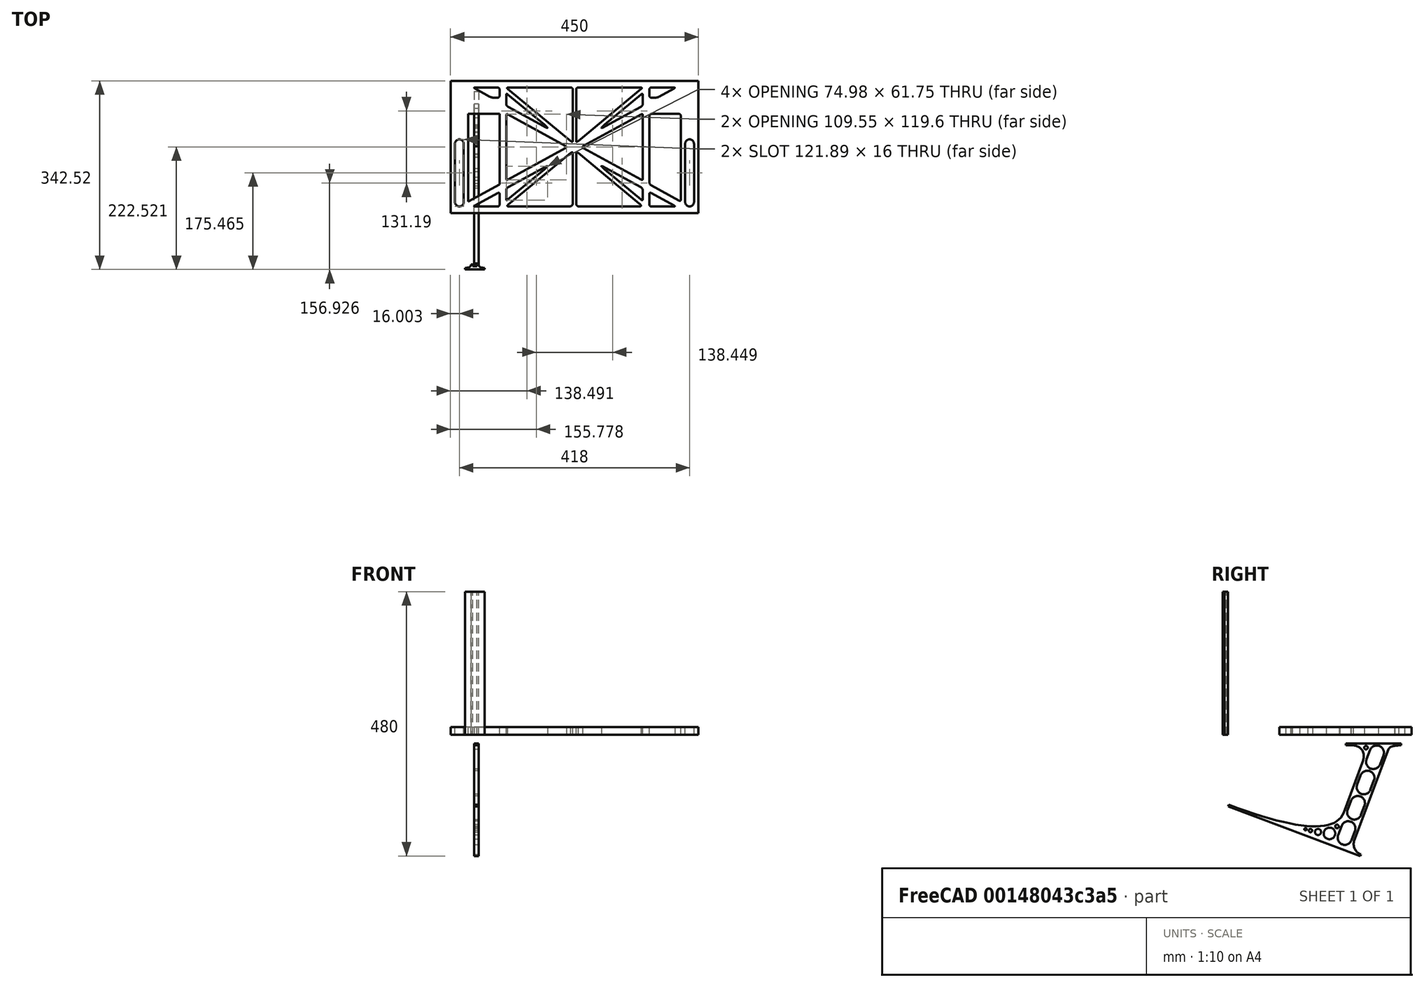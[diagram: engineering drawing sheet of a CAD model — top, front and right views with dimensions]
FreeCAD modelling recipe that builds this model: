
FCSTD DOCUMENT  (FreeCAD 0.19R0.19.2)
Label: laptopStand139FCStd
License: All rights reserved
LicenseURL: http://en.wikipedia.org/wiki/All_rights_reserved
objects: Sketcher::SketchObject×3, Part::Extrusion×3
note: 6 computed .brp shape members not serialized (recipe doc carries the construction recipe); baked Part::Feature solids carry a one-line shape summary decoded from their .brp

FEATURE [Sketcher::SketchObject] Sketch
  FullyConstrained = true
  sketch-geometry (322):
    g0: LineSegment StartX=-10.9272 StartY=-82.7794 StartZ=0 EndX=46.0728 EndY=-51.4823 EndZ=0
    g1: LineSegment StartX=-10.9272 StartY=76.4095 StartZ=0 EndX=-10.9272 EndY=-82.7794 EndZ=0
    g2: LineSegment StartX=46.0728 StartY=76.4095 StartZ=0 EndX=46.0728 EndY=-51.4823 EndZ=0
    g3: LineSegment StartX=-42.9272 StartY=136.221 StartZ=0 EndX=-42.9272 EndY=-103.779 EndZ=0
    g4: LineSegment StartX=407.073 StartY=136.221 StartZ=0 EndX=407.073 EndY=-103.779 EndZ=0
    g5: ArcOfCircle CenterX=-26.9272 CenterY=-83.7794 CenterZ=0 NormalX=0 NormalY=0 NormalZ=1 AngleXU=0 Radius=8 StartAngle=3.14159 EndAngle=6.28319
    g6: ArcOfCircle CenterX=391.073 CenterY=22.1087 CenterZ=0 NormalX=0 NormalY=0 NormalZ=1 AngleXU=0 Radius=8 StartAngle=-4.4e-15 EndAngle=3.14159
    g7: LineSegment StartX=399.073 StartY=22.1087 StartZ=0 EndX=399.073 EndY=-83.7794 EndZ=0
    g8: LineSegment StartX=383.073 StartY=22.1087 StartZ=0 EndX=383.073 EndY=-83.7794 EndZ=0
    g9: ArcOfCircle CenterX=391.073 CenterY=-83.7794 CenterZ=0 NormalX=0 NormalY=0 NormalZ=1 AngleXU=0 Radius=8 StartAngle=3.14159 EndAngle=6.28319
    g10: Circle CenterX=175.022 CenterY=27.0628 CenterZ=0 NormalX=0 NormalY=0 NormalZ=1 AngleXU=0 Radius=1
    g11: Circle CenterX=179.022 CenterY=24.8665 CenterZ=0 NormalX=0 NormalY=0 NormalZ=1 AngleXU=0 Radius=1
    g12: Circle CenterX=179.022 CenterY=27.0628 CenterZ=0 NormalX=0 NormalY=0 NormalZ=1 AngleXU=0 Radius=1
    g13: BSplineCurve PolesCount=3 KnotsCount=2 Degree=2 IsPeriodic=0
    g14: GeomPoint X=175.022 Y=27.0628 Z=0
    g15: GeomPoint X=179.022 Y=27.0628 Z=0
    g16: Circle CenterX=189.124 CenterY=27.0628 CenterZ=0 NormalX=0 NormalY=0 NormalZ=1 AngleXU=0 Radius=1
    g17: Circle CenterX=185.124 CenterY=24.8665 CenterZ=0 NormalX=0 NormalY=0 NormalZ=1 AngleXU=0 Radius=1
    g18: Circle CenterX=185.124 CenterY=27.0628 CenterZ=0 NormalX=0 NormalY=0 NormalZ=1 AngleXU=0 Radius=1
    g19: BSplineCurve PolesCount=3 KnotsCount=2 Degree=2 IsPeriodic=0
    g20: GeomPoint X=189.124 Y=27.0628 Z=0
    g21: GeomPoint X=185.124 Y=27.0628 Z=0
    g22: Circle CenterX=175.022 CenterY=5.37834 CenterZ=0 NormalX=0 NormalY=0 NormalZ=1 AngleXU=0 Radius=1
    g23: Circle CenterX=179.022 CenterY=7.57463 CenterZ=0 NormalX=0 NormalY=0 NormalZ=1 AngleXU=0 Radius=1
    g24: Circle CenterX=179.022 CenterY=5.34704 CenterZ=0 NormalX=0 NormalY=0 NormalZ=1 AngleXU=0 Radius=1
    g25: BSplineCurve PolesCount=3 KnotsCount=2 Degree=2 IsPeriodic=0
    g26: GeomPoint X=175.022 Y=5.37834 Z=0
    g27: GeomPoint X=179.022 Y=5.34704 Z=0
    g28: Circle CenterX=189.124 CenterY=5.37834 CenterZ=0 NormalX=0 NormalY=0 NormalZ=1 AngleXU=0 Radius=1
    g29: Circle CenterX=185.124 CenterY=7.57463 CenterZ=0 NormalX=0 NormalY=0 NormalZ=1 AngleXU=0 Radius=1
    g30: Circle CenterX=185.124 CenterY=5.34704 CenterZ=0 NormalX=0 NormalY=0 NormalZ=1 AngleXU=0 Radius=1
    g31: BSplineCurve PolesCount=3 KnotsCount=2 Degree=2 IsPeriodic=0
    g32: GeomPoint X=189.124 Y=5.37834 Z=0
    g33: GeomPoint X=185.124 Y=5.34704 Z=0
    g34: Circle CenterX=165.871 CenterY=18.1458 CenterZ=0 NormalX=0 NormalY=0 NormalZ=1 AngleXU=0 Radius=1
    g35: Circle CenterX=169.377 CenterY=16.2206 CenterZ=0 NormalX=0 NormalY=0 NormalZ=1 AngleXU=0 Radius=1
    g36: Circle CenterX=165.871 CenterY=14.2954 CenterZ=0 NormalX=0 NormalY=0 NormalZ=1 AngleXU=0 Radius=1
    g37: BSplineCurve PolesCount=3 KnotsCount=2 Degree=2 IsPeriodic=0
    g38: GeomPoint X=165.871 Y=18.1458 Z=0
    g39: GeomPoint X=165.871 Y=14.2954 Z=0
    g40: Circle CenterX=198.275 CenterY=18.1458 CenterZ=0 NormalX=0 NormalY=0 NormalZ=1 AngleXU=0 Radius=1
    g41: Circle CenterX=194.768 CenterY=16.2206 CenterZ=0 NormalX=0 NormalY=0 NormalZ=1 AngleXU=0 Radius=1
    g42: Circle CenterX=198.275 CenterY=14.2954 CenterZ=0 NormalX=0 NormalY=0 NormalZ=1 AngleXU=0 Radius=1
    g43: BSplineCurve PolesCount=3 KnotsCount=2 Degree=2 IsPeriodic=0
    g44: GeomPoint X=198.275 Y=18.1458 Z=0
    g45: GeomPoint X=198.275 Y=14.2954 Z=0
    g46: LineSegment StartX=407.073 StartY=-103.779 StartZ=0 EndX=-42.9272 EndY=-103.779 EndZ=0
    g47: LineSegment StartX=407.073 StartY=136.221 StartZ=0 EndX=-42.9272 EndY=136.221 EndZ=0
    g48: LineSegment StartX=46.0728 StartY=76.4095 StartZ=0 EndX=-10.9272 EndY=76.4095 EndZ=0
    g49: Circle CenterX=125.607 CenterY=54.1951 CenterZ=0 NormalX=0 NormalY=0 NormalZ=1 AngleXU=0 Radius=1
    g50: Circle CenterX=139.632 CenterY=46.4944 CenterZ=0 NormalX=0 NormalY=0 NormalZ=1 AngleXU=0 Radius=1
    g51: Circle CenterX=127.326 CenterY=56.7187 CenterZ=0 NormalX=0 NormalY=0 NormalZ=1 AngleXU=0 Radius=1
    g52: BSplineCurve PolesCount=3 KnotsCount=2 Degree=2 IsPeriodic=0
    g53: GeomPoint X=125.607 Y=54.1951 Z=0
    g54: GeomPoint X=127.326 Y=56.7187 Z=0
    g55: Circle CenterX=236.821 CenterY=56.7187 CenterZ=0 NormalX=0 NormalY=0 NormalZ=1 AngleXU=0 Radius=1
    g56: Circle CenterX=224.513 CenterY=46.4944 CenterZ=0 NormalX=0 NormalY=0 NormalZ=1 AngleXU=0 Radius=1
    g57: Circle CenterX=238.538 CenterY=54.1951 CenterZ=0 NormalX=0 NormalY=0 NormalZ=1 AngleXU=0 Radius=1
    g58: BSplineCurve PolesCount=3 KnotsCount=2 Degree=2 IsPeriodic=0
    g59: GeomPoint X=236.821 Y=56.7187 Z=0
    g60: GeomPoint X=238.538 Y=54.1951 Z=0
    g61: Circle CenterX=238.538 CenterY=-21.7539 CenterZ=0 NormalX=0 NormalY=0 NormalZ=1 AngleXU=0 Radius=1
    g62: Circle CenterX=224.513 CenterY=-14.0532 CenterZ=0 NormalX=0 NormalY=0 NormalZ=1 AngleXU=0 Radius=1
    g63: Circle CenterX=236.821 CenterY=-24.2775 CenterZ=0 NormalX=0 NormalY=0 NormalZ=1 AngleXU=0 Radius=1
    g64: BSplineCurve PolesCount=3 KnotsCount=2 Degree=2 IsPeriodic=0
    g65: GeomPoint X=238.538 Y=-21.7539 Z=0
    g66: GeomPoint X=236.821 Y=-24.2775 Z=0
    g67: Circle CenterX=125.607 CenterY=-21.7539 CenterZ=0 NormalX=0 NormalY=0 NormalZ=1 AngleXU=0 Radius=1
    g68: Circle CenterX=139.632 CenterY=-14.0532 CenterZ=0 NormalX=0 NormalY=0 NormalZ=1 AngleXU=0 Radius=1
    g69: Circle CenterX=127.325 CenterY=-24.2775 CenterZ=0 NormalX=0 NormalY=0 NormalZ=1 AngleXU=0 Radius=1
    g70: BSplineCurve PolesCount=3 KnotsCount=2 Degree=2 IsPeriodic=0
    g71: GeomPoint X=125.607 Y=-21.7539 Z=0
    g72: GeomPoint X=127.325 Y=-24.2775 Z=0
    g73: Circle CenterX=302.996 CenterY=111.695 CenterZ=0 NormalX=0 NormalY=0 NormalZ=1 AngleXU=0 Radius=1
    g74: Circle CenterX=306.073 CenterY=114.251 CenterZ=0 NormalX=0 NormalY=0 NormalZ=1 AngleXU=0 Radius=1
    g75: Circle CenterX=306.073 CenterY=110.251 CenterZ=0 NormalX=0 NormalY=0 NormalZ=1 AngleXU=0 Radius=1
    g76: BSplineCurve PolesCount=3 KnotsCount=2 Degree=2 IsPeriodic=0
    g77: GeomPoint X=302.996 Y=111.695 Z=0
    g78: GeomPoint X=306.073 Y=110.251 Z=0
    g79: Circle CenterX=306.073 CenterY=95.2763 CenterZ=0 NormalX=0 NormalY=0 NormalZ=1 AngleXU=0 Radius=1
    g80: Circle CenterX=306.073 CenterY=91.2763 CenterZ=0 NormalX=0 NormalY=0 NormalZ=1 AngleXU=0 Radius=1
    g81: Circle CenterX=302.567 CenterY=89.3511 CenterZ=0 NormalX=0 NormalY=0 NormalZ=1 AngleXU=0 Radius=1
    g82: BSplineCurve PolesCount=3 KnotsCount=2 Degree=2 IsPeriodic=0
    g83: GeomPoint X=306.073 Y=95.2763 Z=0
    g84: GeomPoint X=302.567 Y=89.3511 Z=0
    g85: LineSegment StartX=306.073 StartY=110.251 StartZ=0 EndX=306.073 EndY=95.2763 EndZ=0
    g86: LineSegment StartX=302.996 StartY=111.695 StartZ=0 EndX=236.821 EndY=56.7187 EndZ=0
    g87: LineSegment StartX=238.538 StartY=54.1951 StartZ=0 EndX=302.567 EndY=89.3511 EndZ=0
    g88: Circle CenterX=61.1496 CenterY=111.695 CenterZ=0 NormalX=0 NormalY=0 NormalZ=1 AngleXU=0 Radius=1
    g89: Circle CenterX=58.0728 CenterY=114.251 CenterZ=0 NormalX=0 NormalY=0 NormalZ=1 AngleXU=0 Radius=1
    g90: Circle CenterX=58.0728 CenterY=110.251 CenterZ=0 NormalX=0 NormalY=0 NormalZ=1 AngleXU=0 Radius=1
    g91: BSplineCurve PolesCount=3 KnotsCount=2 Degree=2 IsPeriodic=0
    g92: GeomPoint X=61.1496 Y=111.695 Z=0
    g93: GeomPoint X=58.0728 Y=110.251 Z=0
    g94: Circle CenterX=61.5791 CenterY=89.3511 CenterZ=0 NormalX=0 NormalY=0 NormalZ=1 AngleXU=0 Radius=1
    g95: Circle CenterX=58.0728 CenterY=91.2763 CenterZ=0 NormalX=0 NormalY=0 NormalZ=1 AngleXU=0 Radius=1
    g96: Circle CenterX=58.0728 CenterY=95.2763 CenterZ=0 NormalX=0 NormalY=0 NormalZ=1 AngleXU=0 Radius=1
    g97: BSplineCurve PolesCount=3 KnotsCount=2 Degree=2 IsPeriodic=0
    g98: GeomPoint X=61.5791 Y=89.3511 Z=0
    g99: GeomPoint X=58.0728 Y=95.2763 Z=0
    g100: LineSegment StartX=58.0728 StartY=110.251 StartZ=0 EndX=58.0728 EndY=95.2763 EndZ=0
    g101: LineSegment StartX=61.1496 StartY=111.695 StartZ=0 EndX=127.326 EndY=56.7187 EndZ=0
    g102: LineSegment StartX=125.607 StartY=54.1951 StartZ=0 EndX=61.5791 EndY=89.3511 EndZ=0
    g103: Circle CenterX=61.5791 CenterY=-56.9099 CenterZ=0 NormalX=0 NormalY=0 NormalZ=1 AngleXU=0 Radius=1
    g104: Circle CenterX=58.0728 CenterY=-58.8351 CenterZ=0 NormalX=0 NormalY=0 NormalZ=1 AngleXU=0 Radius=1
    g105: Circle CenterX=58.0728 CenterY=-62.8351 CenterZ=0 NormalX=0 NormalY=0 NormalZ=1 AngleXU=0 Radius=1
    g106: BSplineCurve PolesCount=3 KnotsCount=2 Degree=2 IsPeriodic=0
    g107: GeomPoint X=61.5791 Y=-56.9099 Z=0
    g108: GeomPoint X=58.0728 Y=-62.8351 Z=0
    g109: Circle CenterX=58.0728 CenterY=-77.8102 CenterZ=0 NormalX=0 NormalY=0 NormalZ=1 AngleXU=0 Radius=1
    g110: Circle CenterX=58.0728 CenterY=-81.8102 CenterZ=0 NormalX=0 NormalY=0 NormalZ=1 AngleXU=0 Radius=1
    g111: Circle CenterX=61.1496 CenterY=-79.2541 CenterZ=0 NormalX=0 NormalY=0 NormalZ=1 AngleXU=0 Radius=1
    g112: BSplineCurve PolesCount=3 KnotsCount=2 Degree=2 IsPeriodic=0
    g113: GeomPoint X=58.0728 Y=-77.8102 Z=0
    g114: GeomPoint X=61.1496 Y=-79.2541 Z=0
    g115: LineSegment StartX=58.0728 StartY=-62.8351 StartZ=0 EndX=58.0728 EndY=-77.8102 EndZ=0
    g116: LineSegment StartX=61.1496 StartY=-79.2541 StartZ=0 EndX=127.325 EndY=-24.2775 EndZ=0
    g117: LineSegment StartX=125.607 StartY=-21.7539 StartZ=0 EndX=61.5791 EndY=-56.9099 EndZ=0
    g118: Circle CenterX=302.567 CenterY=-56.9099 CenterZ=0 NormalX=0 NormalY=0 NormalZ=1 AngleXU=0 Radius=1
    g119: Circle CenterX=306.073 CenterY=-58.8351 CenterZ=0 NormalX=0 NormalY=0 NormalZ=1 AngleXU=0 Radius=1
    g120: Circle CenterX=306.073 CenterY=-62.8351 CenterZ=0 NormalX=0 NormalY=0 NormalZ=1 AngleXU=0 Radius=1
    g121: BSplineCurve PolesCount=3 KnotsCount=2 Degree=2 IsPeriodic=0
    g122: GeomPoint X=302.567 Y=-56.9099 Z=0
    g123: GeomPoint X=306.073 Y=-62.8351 Z=0
    g124: Circle CenterX=302.996 CenterY=-79.2541 CenterZ=0 NormalX=0 NormalY=0 NormalZ=1 AngleXU=0 Radius=1
    g125: Circle CenterX=306.073 CenterY=-81.8102 CenterZ=0 NormalX=0 NormalY=0 NormalZ=1 AngleXU=0 Radius=1
    g126: Circle CenterX=306.073 CenterY=-77.8102 CenterZ=0 NormalX=0 NormalY=0 NormalZ=1 AngleXU=0 Radius=1
    g127: BSplineCurve PolesCount=3 KnotsCount=2 Degree=2 IsPeriodic=0
    g128: GeomPoint X=302.996 Y=-79.2541 Z=0
    g129: GeomPoint X=306.073 Y=-77.8102 Z=0
    g130: LineSegment StartX=306.073 StartY=-62.8351 StartZ=0 EndX=306.073 EndY=-77.8102 EndZ=0
    g131: LineSegment StartX=302.996 StartY=-79.2541 StartZ=0 EndX=236.821 EndY=-24.2775 EndZ=0
    g132: LineSegment StartX=238.538 StartY=-21.7539 StartZ=0 EndX=302.567 EndY=-56.9099 EndZ=0
    g133: Circle CenterX=61.6457 CenterY=-88.8112 CenterZ=0 NormalX=0 NormalY=0 NormalZ=1 AngleXU=0 Radius=1
    g134: Circle CenterX=58.0728 CenterY=-91.7794 CenterZ=0 NormalX=0 NormalY=0 NormalZ=1 AngleXU=0 Radius=1
    g135: Circle CenterX=63.9135 CenterY=-91.7794 CenterZ=0 NormalX=0 NormalY=0 NormalZ=1 AngleXU=0 Radius=1
    g136: BSplineCurve PolesCount=3 KnotsCount=2 Degree=2 IsPeriodic=0
    g137: GeomPoint X=61.6457 Y=-88.8112 Z=0
    g138: GeomPoint X=63.9135 Y=-91.7794 Z=0
    g139: Circle CenterX=179.022 CenterY=-85.8163 CenterZ=0 NormalX=0 NormalY=0 NormalZ=1 AngleXU=0 Radius=1
    g140: Circle CenterX=179.022 CenterY=-91.7794 CenterZ=0 NormalX=0 NormalY=0 NormalZ=1 AngleXU=0 Radius=1
    g141: Circle CenterX=171.895 CenterY=-91.7794 CenterZ=0 NormalX=0 NormalY=0 NormalZ=1 AngleXU=0 Radius=1
    g142: BSplineCurve PolesCount=3 KnotsCount=2 Degree=2 IsPeriodic=0
    g143: GeomPoint X=179.022 Y=-85.8163 Z=0
    g144: GeomPoint X=171.895 Y=-91.7794 Z=0
    g145: Circle CenterX=185.124 CenterY=-86.2028 CenterZ=0 NormalX=0 NormalY=0 NormalZ=1 AngleXU=0 Radius=1
    g146: Circle CenterX=185.124 CenterY=-91.7794 CenterZ=0 NormalX=0 NormalY=0 NormalZ=1 AngleXU=0 Radius=1
    g147: Circle CenterX=191.747 CenterY=-91.7794 CenterZ=0 NormalX=0 NormalY=0 NormalZ=1 AngleXU=0 Radius=1
    g148: BSplineCurve PolesCount=3 KnotsCount=2 Degree=2 IsPeriodic=0
    g149: GeomPoint X=185.124 Y=-86.2028 Z=0
    g150: GeomPoint X=191.747 Y=-91.7794 Z=0
    g151: Circle CenterX=299.888 CenterY=-86.6413 CenterZ=0 NormalX=0 NormalY=0 NormalZ=1 AngleXU=0 Radius=1
    g152: Circle CenterX=306.073 CenterY=-91.7794 CenterZ=0 NormalX=0 NormalY=0 NormalZ=1 AngleXU=0 Radius=1
    g153: Circle CenterX=298.776 CenterY=-91.7794 CenterZ=0 NormalX=0 NormalY=0 NormalZ=1 AngleXU=0 Radius=1
    g154: BSplineCurve PolesCount=3 KnotsCount=2 Degree=2 IsPeriodic=0
    g155: GeomPoint X=299.888 Y=-86.6413 Z=0
    g156: GeomPoint X=298.776 Y=-91.7794 Z=0
    g157: LineSegment StartX=189.124 StartY=5.37834 StartZ=0 EndX=299.888 EndY=-86.6413 EndZ=0
    g158: LineSegment StartX=298.776 StartY=-91.7794 StartZ=0 EndX=191.747 EndY=-91.7794 EndZ=0
    g159: LineSegment StartX=185.124 StartY=-86.2028 StartZ=0 EndX=185.124 EndY=5.34704 EndZ=0
    g160: LineSegment StartX=179.022 StartY=5.34704 StartZ=0 EndX=179.022 EndY=-85.8163 EndZ=0
    g161: LineSegment StartX=171.895 StartY=-91.7794 StartZ=0 EndX=63.9135 EndY=-91.7794 EndZ=0
    g162: LineSegment StartX=61.6457 StartY=-88.8112 StartZ=0 EndX=175.022 EndY=5.37834 EndZ=0
    g163: Circle CenterX=302.073 CenterY=124.221 CenterZ=0 NormalX=0 NormalY=0 NormalZ=1 AngleXU=0 Radius=1
    g164: Circle CenterX=306.073 CenterY=124.221 CenterZ=0 NormalX=0 NormalY=0 NormalZ=1 AngleXU=0 Radius=1
    g165: Circle CenterX=302.996 CenterY=121.665 CenterZ=0 NormalX=0 NormalY=0 NormalZ=1 AngleXU=0 Radius=1
    g166: BSplineCurve PolesCount=3 KnotsCount=2 Degree=2 IsPeriodic=0
    g167: GeomPoint X=302.073 Y=124.221 Z=0
    g168: GeomPoint X=302.996 Y=121.665 Z=0
    g169: Circle CenterX=189.124 CenterY=124.221 CenterZ=0 NormalX=0 NormalY=0 NormalZ=1 AngleXU=0 Radius=1
    g170: Circle CenterX=185.124 CenterY=124.221 CenterZ=0 NormalX=0 NormalY=0 NormalZ=1 AngleXU=0 Radius=1
    g171: Circle CenterX=185.124 CenterY=120.221 CenterZ=0 NormalX=0 NormalY=0 NormalZ=1 AngleXU=0 Radius=1
    g172: BSplineCurve PolesCount=3 KnotsCount=2 Degree=2 IsPeriodic=0
    g173: GeomPoint X=189.124 Y=124.221 Z=0
    g174: GeomPoint X=185.124 Y=120.221 Z=0
    g175: Circle CenterX=175.022 CenterY=124.221 CenterZ=0 NormalX=0 NormalY=0 NormalZ=1 AngleXU=0 Radius=1
    g176: Circle CenterX=179.022 CenterY=124.221 CenterZ=0 NormalX=0 NormalY=0 NormalZ=1 AngleXU=0 Radius=1
    g177: Circle CenterX=179.022 CenterY=120.221 CenterZ=0 NormalX=0 NormalY=0 NormalZ=1 AngleXU=0 Radius=1
    g178: BSplineCurve PolesCount=3 KnotsCount=2 Degree=2 IsPeriodic=0
    g179: GeomPoint X=175.022 Y=124.221 Z=0
    g180: GeomPoint X=179.022 Y=120.221 Z=0
    g181: Circle CenterX=62.0728 CenterY=124.221 CenterZ=0 NormalX=0 NormalY=0 NormalZ=1 AngleXU=0 Radius=1
    g182: Circle CenterX=58.0728 CenterY=124.221 CenterZ=0 NormalX=0 NormalY=0 NormalZ=1 AngleXU=0 Radius=1
    g183: Circle CenterX=61.1496 CenterY=121.665 CenterZ=0 NormalX=0 NormalY=0 NormalZ=1 AngleXU=0 Radius=1
    g184: BSplineCurve PolesCount=3 KnotsCount=2 Degree=2 IsPeriodic=0
    g185: GeomPoint X=62.0728 Y=124.221 Z=0
    g186: GeomPoint X=61.1496 Y=121.665 Z=0
    g187: LineSegment StartX=62.0728 StartY=124.221 StartZ=0 EndX=175.022 EndY=124.221 EndZ=0
    g188: LineSegment StartX=179.022 StartY=120.221 StartZ=0 EndX=179.022 EndY=27.0628 EndZ=0
    g189: LineSegment StartX=185.124 StartY=27.0628 StartZ=0 EndX=185.124 EndY=120.221 EndZ=0
    g190: LineSegment StartX=189.124 StartY=124.221 StartZ=0 EndX=302.073 EndY=124.221 EndZ=0
    g191: LineSegment StartX=302.996 StartY=121.665 StartZ=0 EndX=189.124 EndY=27.0628 EndZ=0
    g192: LineSegment StartX=175.022 StartY=27.0628 StartZ=0 EndX=61.1496 EndY=121.665 EndZ=0
    g193: Circle CenterX=61.5791 CenterY=75.4095 CenterZ=0 NormalX=0 NormalY=0 NormalZ=1 AngleXU=0 Radius=1
    g194: Circle CenterX=58.0728 CenterY=77.3346 CenterZ=0 NormalX=0 NormalY=0 NormalZ=1 AngleXU=0 Radius=1
    g195: Circle CenterX=58.0728 CenterY=73.3346 CenterZ=0 NormalX=0 NormalY=0 NormalZ=1 AngleXU=0 Radius=1
    g196: BSplineCurve PolesCount=3 KnotsCount=2 Degree=2 IsPeriodic=0
    g197: GeomPoint X=61.5791 Y=75.4095 Z=0
    g198: GeomPoint X=58.0728 Y=73.3346 Z=0
    g199: Circle CenterX=58.0728 CenterY=-40.8935 CenterZ=0 NormalX=0 NormalY=0 NormalZ=1 AngleXU=0 Radius=1
    g200: Circle CenterX=58.0728 CenterY=-44.8935 CenterZ=0 NormalX=0 NormalY=0 NormalZ=1 AngleXU=0 Radius=1
    g201: Circle CenterX=61.5791 CenterY=-42.9683 CenterZ=0 NormalX=0 NormalY=0 NormalZ=1 AngleXU=0 Radius=1
    g202: BSplineCurve PolesCount=3 KnotsCount=2 Degree=2 IsPeriodic=0
    g203: GeomPoint X=58.0728 Y=-40.8935 Z=0
    g204: GeomPoint X=61.5791 Y=-42.9683 Z=0
    g205: LineSegment StartX=61.5791 StartY=-42.9683 StartZ=0 EndX=165.871 EndY=14.2954 EndZ=0
    g206: LineSegment StartX=165.871 StartY=18.1458 StartZ=0 EndX=61.5791 EndY=75.4095 EndZ=0
    g207: LineSegment StartX=58.0728 StartY=73.3346 StartZ=0 EndX=58.0728 EndY=-40.8935 EndZ=0
    g208: Circle CenterX=302.567 CenterY=-42.9683 CenterZ=0 NormalX=0 NormalY=0 NormalZ=1 AngleXU=0 Radius=1
    g209: Circle CenterX=306.073 CenterY=-44.8935 CenterZ=0 NormalX=0 NormalY=0 NormalZ=1 AngleXU=0 Radius=1
    g210: Circle CenterX=306.073 CenterY=-40.8935 CenterZ=0 NormalX=0 NormalY=0 NormalZ=1 AngleXU=0 Radius=1
    g211: BSplineCurve PolesCount=3 KnotsCount=2 Degree=2 IsPeriodic=0
    g212: GeomPoint X=302.567 Y=-42.9683 Z=0
    g213: GeomPoint X=306.073 Y=-40.8935 Z=0
    g214: Circle CenterX=306.073 CenterY=73.3346 CenterZ=0 NormalX=0 NormalY=0 NormalZ=1 AngleXU=0 Radius=1
    g215: Circle CenterX=306.073 CenterY=77.3346 CenterZ=0 NormalX=0 NormalY=0 NormalZ=1 AngleXU=0 Radius=1
    g216: Circle CenterX=302.567 CenterY=75.4095 CenterZ=0 NormalX=0 NormalY=0 NormalZ=1 AngleXU=0 Radius=1
    g217: BSplineCurve PolesCount=3 KnotsCount=2 Degree=2 IsPeriodic=0
    g218: GeomPoint X=306.073 Y=73.3346 Z=0
    g219: GeomPoint X=302.567 Y=75.4095 Z=0
    g220: LineSegment StartX=302.567 StartY=-42.9683 StartZ=0 EndX=198.275 EndY=14.2954 EndZ=0
    g221: LineSegment StartX=198.275 StartY=18.1458 StartZ=0 EndX=302.567 EndY=75.4095 EndZ=0
    g222: LineSegment StartX=306.073 StartY=73.3346 StartZ=0 EndX=306.073 EndY=-40.8935 EndZ=0
    g223: LineSegment StartX=322.073 StartY=105.865 StartZ=0 EndX=328.643 EndY=105.865 EndZ=0
    g224: LineSegment StartX=318.073 StartY=120.221 StartZ=0 EndX=318.073 EndY=109.865 EndZ=0
    g225: LineSegment StartX=336.157 StartY=107.779 StartZ=0 EndX=362.567 EndY=122.294 EndZ=0
    g226: Circle CenterX=362.073 CenterY=124.221 CenterZ=0 NormalX=0 NormalY=0 NormalZ=1 AngleXU=0 Radius=1
    g227: Circle CenterX=366.073 CenterY=124.221 CenterZ=0 NormalX=0 NormalY=0 NormalZ=1 AngleXU=0 Radius=1
    g228: Circle CenterX=362.567 CenterY=122.294 CenterZ=0 NormalX=0 NormalY=0 NormalZ=1 AngleXU=0 Radius=1
    g229: BSplineCurve PolesCount=3 KnotsCount=2 Degree=2 IsPeriodic=0
    g230: GeomPoint X=362.073 Y=124.221 Z=0
    g231: GeomPoint X=362.567 Y=122.294 Z=0
    g232: Circle CenterX=322.073 CenterY=124.221 CenterZ=0 NormalX=0 NormalY=0 NormalZ=1 AngleXU=0 Radius=1
    g233: Circle CenterX=318.073 CenterY=124.221 CenterZ=0 NormalX=0 NormalY=0 NormalZ=1 AngleXU=0 Radius=1
    g234: Circle CenterX=318.073 CenterY=120.221 CenterZ=0 NormalX=0 NormalY=0 NormalZ=1 AngleXU=0 Radius=1
    g235: BSplineCurve PolesCount=3 KnotsCount=2 Degree=2 IsPeriodic=0
    g236: GeomPoint X=322.073 Y=124.221 Z=0
    g237: GeomPoint X=318.073 Y=120.221 Z=0
    g238: Circle CenterX=322.073 CenterY=105.865 CenterZ=0 NormalX=0 NormalY=0 NormalZ=1 AngleXU=0 Radius=1
    g239: Circle CenterX=318.073 CenterY=105.865 CenterZ=0 NormalX=0 NormalY=0 NormalZ=1 AngleXU=0 Radius=1
    g240: Circle CenterX=318.073 CenterY=109.865 CenterZ=0 NormalX=0 NormalY=0 NormalZ=1 AngleXU=0 Radius=1
    g241: BSplineCurve PolesCount=3 KnotsCount=2 Degree=2 IsPeriodic=0
    g242: GeomPoint X=322.073 Y=105.865 Z=0
    g243: GeomPoint X=318.073 Y=109.865 Z=0
    g244: Circle CenterX=336.157 CenterY=107.779 CenterZ=0 NormalX=0 NormalY=0 NormalZ=1 AngleXU=0 Radius=1
    g245: Circle CenterX=332.651 CenterY=105.853 CenterZ=0 NormalX=0 NormalY=0 NormalZ=1 AngleXU=0 Radius=1
    g246: Circle CenterX=328.643 CenterY=105.865 CenterZ=0 NormalX=0 NormalY=0 NormalZ=1 AngleXU=0 Radius=1
    g247: BSplineCurve PolesCount=3 KnotsCount=2 Degree=2 IsPeriodic=0
    g248: GeomPoint X=336.157 Y=107.779 Z=0
    g249: GeomPoint X=328.643 Y=105.865 Z=0
    g250: LineSegment StartX=322.073 StartY=124.221 StartZ=0 EndX=362.073 EndY=124.221 EndZ=0
    g251: Circle CenterX=371.567 CenterY=-80.8644 CenterZ=0 NormalX=0 NormalY=0 NormalZ=1 AngleXU=0 Radius=1
    g252: Circle CenterX=375.073 CenterY=-82.7896 CenterZ=0 NormalX=0 NormalY=0 NormalZ=1 AngleXU=0 Radius=1
    g253: Circle CenterX=375.073 CenterY=-78.7896 CenterZ=0 NormalX=0 NormalY=0 NormalZ=1 AngleXU=0 Radius=1
    g254: BSplineCurve PolesCount=3 KnotsCount=2 Degree=2 IsPeriodic=0
    g255: GeomPoint X=371.567 Y=-80.8644 Z=0
    g256: GeomPoint X=375.073 Y=-78.7896 Z=0
    g257: Circle CenterX=321.579 CenterY=-53.4075 CenterZ=0 NormalX=0 NormalY=0 NormalZ=1 AngleXU=0 Radius=1
    g258: Circle CenterX=318.073 CenterY=-51.4823 CenterZ=0 NormalX=0 NormalY=0 NormalZ=1 AngleXU=0 Radius=1
    g259: Circle CenterX=318.073 CenterY=-47.4805 CenterZ=0 NormalX=0 NormalY=0 NormalZ=1 AngleXU=0 Radius=1
    g260: BSplineCurve PolesCount=3 KnotsCount=2 Degree=2 IsPeriodic=0
    g261: GeomPoint X=321.579 Y=-53.4075 Z=0
    g262: GeomPoint X=318.073 Y=-47.4805 Z=0
    g263: LineSegment StartX=371.567 StartY=-80.8644 StartZ=0 EndX=321.579 EndY=-53.4075 EndZ=0
    g264: Circle CenterX=321.579 CenterY=-67.3492 CenterZ=0 NormalX=0 NormalY=0 NormalZ=1 AngleXU=0 Radius=1
    g265: Circle CenterX=318.073 CenterY=-65.424 CenterZ=0 NormalX=0 NormalY=0 NormalZ=1 AngleXU=0 Radius=1
    g266: Circle CenterX=318.073 CenterY=-69.424 CenterZ=0 NormalX=0 NormalY=0 NormalZ=1 AngleXU=0 Radius=1
    g267: BSplineCurve PolesCount=3 KnotsCount=2 Degree=2 IsPeriodic=0
    g268: GeomPoint X=321.579 Y=-67.3492 Z=0
    g269: GeomPoint X=318.073 Y=-69.424 Z=0
    g270: Circle CenterX=362.567 CenterY=-89.8542 CenterZ=0 NormalX=0 NormalY=0 NormalZ=1 AngleXU=0 Radius=1
    g271: Circle CenterX=366.073 CenterY=-91.7794 CenterZ=0 NormalX=0 NormalY=0 NormalZ=1 AngleXU=0 Radius=1
    g272: Circle CenterX=362.073 CenterY=-91.7794 CenterZ=0 NormalX=0 NormalY=0 NormalZ=1 AngleXU=0 Radius=1
    g273: BSplineCurve PolesCount=3 KnotsCount=2 Degree=2 IsPeriodic=0
    g274: GeomPoint X=362.567 Y=-89.8542 Z=0
    g275: GeomPoint X=362.073 Y=-91.7794 Z=0
    g276: Circle CenterX=322.073 CenterY=-91.7794 CenterZ=0 NormalX=0 NormalY=0 NormalZ=1 AngleXU=0 Radius=1
    g277: Circle CenterX=318.073 CenterY=-91.7794 CenterZ=0 NormalX=0 NormalY=0 NormalZ=1 AngleXU=0 Radius=1
    g278: Circle CenterX=318.073 CenterY=-87.7794 CenterZ=0 NormalX=0 NormalY=0 NormalZ=1 AngleXU=0 Radius=1
    g279: BSplineCurve PolesCount=3 KnotsCount=2 Degree=2 IsPeriodic=0
    g280: GeomPoint X=322.073 Y=-91.7794 Z=0
    g281: GeomPoint X=318.073 Y=-87.7794 Z=0
    g282: LineSegment StartX=362.567 StartY=-89.8542 StartZ=0 EndX=321.579 EndY=-67.3492 EndZ=0
    g283: LineSegment StartX=318.073 StartY=-69.424 StartZ=0 EndX=318.073 EndY=-87.7794 EndZ=0
    g284: LineSegment StartX=322.073 StartY=-91.7794 StartZ=0 EndX=362.073 EndY=-91.7794 EndZ=0
    g285: Circle CenterX=42.5666 CenterY=-67.3492 CenterZ=0 NormalX=0 NormalY=0 NormalZ=1 AngleXU=0 Radius=1
    g286: Circle CenterX=46.0728 CenterY=-65.424 CenterZ=0 NormalX=0 NormalY=0 NormalZ=1 AngleXU=0 Radius=1
    g287: Circle CenterX=46.0728 CenterY=-69.424 CenterZ=0 NormalX=0 NormalY=0 NormalZ=1 AngleXU=0 Radius=1
    g288: BSplineCurve PolesCount=3 KnotsCount=2 Degree=2 IsPeriodic=0
    g289: GeomPoint X=42.5666 Y=-67.3492 Z=0
    g290: GeomPoint X=46.0728 Y=-69.424 Z=0
    g291: Circle CenterX=46.0728 CenterY=-87.7794 CenterZ=0 NormalX=0 NormalY=0 NormalZ=1 AngleXU=0 Radius=1
    g292: Circle CenterX=46.0728 CenterY=-91.7794 CenterZ=0 NormalX=0 NormalY=0 NormalZ=1 AngleXU=0 Radius=1
    g293: Circle CenterX=42.0728 CenterY=-91.7794 CenterZ=0 NormalX=0 NormalY=0 NormalZ=1 AngleXU=0 Radius=1
    g294: BSplineCurve PolesCount=3 KnotsCount=2 Degree=2 IsPeriodic=0
    g295: GeomPoint X=46.0728 Y=-87.7794 Z=0
    g296: GeomPoint X=42.0728 Y=-91.7794 Z=0
    g297: Circle CenterX=2.07281 CenterY=-91.7794 CenterZ=0 NormalX=0 NormalY=0 NormalZ=1 AngleXU=0 Radius=1
    g298: Circle CenterX=-1.92719 CenterY=-91.7794 CenterZ=0 NormalX=0 NormalY=0 NormalZ=1 AngleXU=0 Radius=1
    g299: Circle CenterX=1.57905 CenterY=-89.8542 CenterZ=0 NormalX=0 NormalY=0 NormalZ=1 AngleXU=0 Radius=1
    g300: BSplineCurve PolesCount=3 KnotsCount=2 Degree=2 IsPeriodic=0
    g301: GeomPoint X=2.07281 Y=-91.7794 Z=0
    g302: GeomPoint X=1.57905 Y=-89.8542 Z=0
    g303: LineSegment StartX=2.07281 StartY=-91.7794 StartZ=0 EndX=42.0728 EndY=-91.7794 EndZ=0
    g304: LineSegment StartX=46.0728 StartY=-87.7794 StartZ=0 EndX=46.0728 EndY=-69.424 EndZ=0
    g305: LineSegment StartX=42.5666 StartY=-67.3492 StartZ=0 EndX=1.57905 EndY=-89.8542 EndZ=0
    g306: Circle CenterX=322.073 CenterY=76.4095 CenterZ=0 NormalX=0 NormalY=0 NormalZ=1 AngleXU=0 Radius=4
    g307: BSplineCurve PolesCount=3 KnotsCount=2 Degree=2 IsPeriodic=0
    g308: GeomPoint X=318.073 Y=72.4095 Z=0
    g309: GeomPoint X=322.073 Y=76.4095 Z=0
    g310: Circle CenterX=375.073 CenterY=72.4095 CenterZ=0 NormalX=0 NormalY=0 NormalZ=1 AngleXU=0 Radius=1
    g311: Circle CenterX=375.073 CenterY=76.4095 CenterZ=0 NormalX=0 NormalY=0 NormalZ=1 AngleXU=0 Radius=1
    g312: Circle CenterX=371.073 CenterY=76.4095 CenterZ=0 NormalX=0 NormalY=0 NormalZ=1 AngleXU=0 Radius=1
    g313: BSplineCurve PolesCount=3 KnotsCount=2 Degree=2 IsPeriodic=0
    g314: GeomPoint X=375.073 Y=72.4095 Z=0
    g315: GeomPoint X=371.073 Y=76.4095 Z=0
    g316: LineSegment StartX=322.073 StartY=76.4095 StartZ=0 EndX=371.073 EndY=76.4095 EndZ=0
    g317: LineSegment StartX=318.073 StartY=72.4095 StartZ=0 EndX=318.073 EndY=-47.4805 EndZ=0
    g318: LineSegment StartX=375.073 StartY=72.4095 StartZ=0 EndX=375.073 EndY=-78.7896 EndZ=0
    g319: ArcOfCircle CenterX=-26.9272 CenterY=22.1087 CenterZ=0 NormalX=0 NormalY=0 NormalZ=1 AngleXU=0 Radius=4 StartAngle=5e-16 EndAngle=3.14159
    g320: LineSegment StartX=-30.9272 StartY=22.1087 StartZ=0 EndX=-34.9272 EndY=-83.7794 EndZ=0
    g321: LineSegment StartX=-18.9272 StartY=-83.7794 StartZ=0 EndX=-22.9272 EndY=22.1087 EndZ=0
  constraints (531):
    c: Coincident(g0,g2)
    c: Block(g0)
    c: Block(g1)
    c: Vertical(g3)
    c: Vertical(g4)
    c: Block(g4)
    c: Block(g3)
    c: Tangent(g6,g7) = 1.5708
    c: Tangent(g7,g9) = 1.5708
    c: Equal(g6,g9)
    c: Coincident(g8,g6)
    c: Coincident(g8,g9)
    c: Block(g7)
    c: Block(g8)
    c: Weight(g10) = 1
    c: Equal(g10,g11)
    c: Equal(g10,g12)
    c: InternalAlignment(g10,g13)
    c: InternalAlignment(g11,g13)
    c: InternalAlignment(g12,g13)
    c: InternalAlignment(g14,g13)
    c: InternalAlignment(g15,g13)
    c: Weight(g16) = 1
    c: Equal(g16,g17)
    c: Equal(g16,g18)
    c: InternalAlignment(g16,g19)
    c: InternalAlignment(g17,g19)
    c: InternalAlignment(g18,g19)
    c: InternalAlignment(g20,g19)
    c: InternalAlignment(g21,g19)
    c: Block(g19)
    c: Block(g13)
    c: Weight(g22) = 1
    c: Equal(g22,g23)
    c: Equal(g22,g24)
    c: InternalAlignment(g22,g25)
    c: InternalAlignment(g23,g25)
    c: InternalAlignment(g24,g25)
    c: InternalAlignment(g26,g25)
    c: InternalAlignment(g27,g25)
    c: Weight(g28) = 1
    c: Equal(g28,g29)
    c: Equal(g28,g30)
    c: InternalAlignment(g28,g31)
    c: InternalAlignment(g29,g31)
    c: InternalAlignment(g30,g31)
    c: InternalAlignment(g32,g31)
    c: InternalAlignment(g33,g31)
    c: Block(g31)
    c: Block(g25)
    c: Weight(g34) = 1
    c: Equal(g34,g35)
    c: Equal(g34,g36)
    c: InternalAlignment(g34,g37)
    c: InternalAlignment(g35,g37)
    c: InternalAlignment(g36,g37)
    c: InternalAlignment(g38,g37)
    c: InternalAlignment(g39,g37)
    c: Weight(g40) = 1
    c: Equal(g40,g41)
    c: Equal(g40,g42)
    c: InternalAlignment(g40,g43)
    c: InternalAlignment(g41,g43)
    c: InternalAlignment(g42,g43)
    c: InternalAlignment(g44,g43)
    c: InternalAlignment(g45,g43)
    c: Block(g37)
    c: Block(g43)
    c: Coincident(g46,g4)
    c: Coincident(g46,g3)
    c: Horizontal(g46)
    c: Distance(g46) = 450
    c: Coincident(g47,g4)
    c: Coincident(g47,g3)
    c: Horizontal(g47)
    c: Horizontal(g48)
    c: Coincident(g2,g48)
    c: Block(g48)
    c: Coincident(g1,g48)
    c: Weight(g49) = 1
    c: Equal(g49,g50)
    c: Equal(g49,g51)
    c: InternalAlignment(g49,g52)
    c: InternalAlignment(g50,g52)
    c: InternalAlignment(g51,g52)
    c: InternalAlignment(g53,g52)
    c: InternalAlignment(g54,g52)
    c: Block(g52)
    c: Weight(g55) = 1
    c: Equal(g55,g56)
    c: Equal(g55,g57)
    c: InternalAlignment(g55,g58)
    c: InternalAlignment(g56,g58)
    c: InternalAlignment(g57,g58)
    c: InternalAlignment(g59,g58)
    c: InternalAlignment(g60,g58)
    c: Block(g58)
    c: Weight(g61) = 1
    c: Equal(g61,g62)
    c: Equal(g61,g63)
    c: InternalAlignment(g61,g64)
    c: InternalAlignment(g62,g64)
    c: InternalAlignment(g63,g64)
    c: InternalAlignment(g65,g64)
    c: InternalAlignment(g66,g64)
    c: Block(g64)
    c: Weight(g67) = 1
    c: Equal(g67,g68)
    c: Equal(g67,g69)
    c: InternalAlignment(g67,g70)
    c: InternalAlignment(g68,g70)
    c: InternalAlignment(g69,g70)
    c: InternalAlignment(g71,g70)
    c: InternalAlignment(g72,g70)
    c: Block(g70)
    c: Weight(g73) = 1
    c: Equal(g73,g74)
    c: Equal(g73,g75)
    c: InternalAlignment(g73,g76)
    c: InternalAlignment(g74,g76)
    c: InternalAlignment(g75,g76)
    c: InternalAlignment(g77,g76)
    c: InternalAlignment(g78,g76)
    c: Weight(g79) = 1
    c: Equal(g79,g80)
    c: Equal(g79,g81)
    c: InternalAlignment(g79,g82)
    c: InternalAlignment(g80,g82)
    c: InternalAlignment(g81,g82)
    c: InternalAlignment(g83,g82)
    c: InternalAlignment(g84,g82)
    c: Block(g76)
    c: Block(g82)
    c: Coincident(g85,g76)
    c: Coincident(g85,g82)
    c: Vertical(g85)
    c: Coincident(g86,g76)
    c: Coincident(g86,g58)
    c: Coincident(g87,g58)
    c: Coincident(g87,g82)
    c: Weight(g88) = 1
    c: Equal(g88,g89)
    c: Equal(g88,g90)
    c: InternalAlignment(g88,g91)
    c: InternalAlignment(g89,g91)
    c: InternalAlignment(g90,g91)
    c: InternalAlignment(g92,g91)
    c: InternalAlignment(g93,g91)
    c: Weight(g94) = 1
    c: Equal(g94,g95)
    c: Equal(g94,g96)
    c: InternalAlignment(g94,g97)
    c: InternalAlignment(g95,g97)
    c: InternalAlignment(g96,g97)
    c: InternalAlignment(g98,g97)
    c: InternalAlignment(g99,g97)
    c: Block(g91)
    c: Block(g97)
    c: Coincident(g100,g91)
    c: Coincident(g100,g97)
    c: Vertical(g100)
    c: Coincident(g101,g91)
    c: Coincident(g101,g52)
    c: Coincident(g102,g52)
    c: Coincident(g102,g97)
    c: Weight(g103) = 1
    c: Equal(g103,g104)
    c: Equal(g103,g105)
    c: InternalAlignment(g103,g106)
    c: InternalAlignment(g104,g106)
    c: InternalAlignment(g105,g106)
    c: InternalAlignment(g107,g106)
    c: InternalAlignment(g108,g106)
    c: Weight(g109) = 1
    c: Equal(g109,g110)
    c: Equal(g109,g111)
    c: InternalAlignment(g109,g112)
    c: InternalAlignment(g110,g112)
    c: InternalAlignment(g111,g112)
    c: InternalAlignment(g113,g112)
    c: InternalAlignment(g114,g112)
    c: Block(g106)
    c: Block(g112)
    c: Coincident(g115,g106)
    c: Coincident(g115,g112)
    c: Vertical(g115)
    c: Coincident(g116,g112)
    c: Coincident(g116,g70)
    c: Coincident(g117,g70)
    c: Coincident(g117,g106)
    c: Weight(g118) = 1
    c: Equal(g118,g119)
    c: Equal(g118,g120)
    c: InternalAlignment(g118,g121)
    c: InternalAlignment(g119,g121)
    c: InternalAlignment(g120,g121)
    c: InternalAlignment(g122,g121)
    c: InternalAlignment(g123,g121)
    c: Weight(g124) = 1
    c: Equal(g124,g125)
    c: Equal(g124,g126)
    c: InternalAlignment(g124,g127)
    c: InternalAlignment(g125,g127)
    c: InternalAlignment(g126,g127)
    c: InternalAlignment(g128,g127)
    c: InternalAlignment(g129,g127)
    c: Block(g121)
    c: Block(g127)
    c: Coincident(g130,g121)
    c: Coincident(g130,g127)
    c: Vertical(g130)
    c: Coincident(g131,g127)
    c: Coincident(g131,g64)
    c: Coincident(g132,g64)
    c: Coincident(g132,g121)
    c: Weight(g133) = 1
    c: Equal(g133,g134)
    c: Equal(g133,g135)
    c: InternalAlignment(g133,g136)
    c: InternalAlignment(g134,g136)
    c: InternalAlignment(g135,g136)
    c: InternalAlignment(g137,g136)
    c: InternalAlignment(g138,g136)
    c: Weight(g139) = 1
    c: Equal(g139,g140)
    c: Equal(g139,g141)
    c: InternalAlignment(g139,g142)
    c: InternalAlignment(g140,g142)
    c: InternalAlignment(g141,g142)
    c: InternalAlignment(g143,g142)
    c: InternalAlignment(g144,g142)
    c: Weight(g145) = 1
    c: Equal(g145,g146)
    c: Equal(g145,g147)
    c: InternalAlignment(g145,g148)
    c: InternalAlignment(g146,g148)
    c: InternalAlignment(g147,g148)
    c: InternalAlignment(g149,g148)
    c: InternalAlignment(g150,g148)
    c: Weight(g151) = 1
    c: Equal(g151,g152)
    c: Equal(g151,g153)
    c: InternalAlignment(g151,g154)
    c: InternalAlignment(g152,g154)
    c: InternalAlignment(g153,g154)
    c: InternalAlignment(g155,g154)
    c: InternalAlignment(g156,g154)
    c: Block(g154)
    c: Block(g148)
    c: Block(g142)
    c: Block(g136)
    c: Coincident(g157,g31)
    c: Coincident(g157,g154)
    c: Coincident(g158,g154)
    c: Coincident(g158,g148)
    c: Horizontal(g158)
    c: Coincident(g159,g148)
    c: Coincident(g159,g31)
    c: Vertical(g159)
    c: Coincident(g160,g25)
    c: Coincident(g160,g142)
    c: Vertical(g160)
    c: Coincident(g161,g142)
    c: Coincident(g161,g136)
    c: Horizontal(g161)
    c: Coincident(g162,g136)
    c: Coincident(g162,g25)
    c: Weight(g163) = 1
    c: Equal(g163,g164)
    c: Equal(g163,g165)
    c: InternalAlignment(g163,g166)
    c: InternalAlignment(g164,g166)
    c: InternalAlignment(g165,g166)
    c: InternalAlignment(g167,g166)
    c: InternalAlignment(g168,g166)
    c: Weight(g169) = 1
    c: Equal(g169,g170)
    c: Equal(g169,g171)
    c: InternalAlignment(g169,g172)
    c: InternalAlignment(g170,g172)
    c: InternalAlignment(g171,g172)
    c: InternalAlignment(g173,g172)
    c: InternalAlignment(g174,g172)
    c: Weight(g175) = 1
    c: Equal(g175,g176)
    c: Equal(g175,g177)
    c: InternalAlignment(g175,g178)
    c: InternalAlignment(g176,g178)
    c: InternalAlignment(g177,g178)
    c: InternalAlignment(g179,g178)
    c: InternalAlignment(g180,g178)
    c: Weight(g181) = 1
    c: Equal(g181,g182)
    c: Equal(g181,g183)
    c: InternalAlignment(g181,g184)
    c: InternalAlignment(g182,g184)
    c: InternalAlignment(g183,g184)
    c: InternalAlignment(g185,g184)
    c: InternalAlignment(g186,g184)
    c: Block(g184)
    c: Block(g178)
    c: Block(g172)
    c: Block(g166)
    c: Coincident(g187,g184)
    c: Coincident(g187,g178)
    c: Horizontal(g187)
    c: Coincident(g188,g178)
    c: Coincident(g188,g13)
    c: Vertical(g188)
    c: Coincident(g189,g19)
    c: Coincident(g189,g172)
    c: Vertical(g189)
    c: Coincident(g190,g172)
    c: Coincident(g190,g166)
    c: Horizontal(g190)
    c: Coincident(g191,g166)
    c: Coincident(g191,g19)
    c: Coincident(g192,g13)
    c: Weight(g193) = 1
    c: Equal(g193,g194)
    c: Equal(g193,g195)
    c: InternalAlignment(g193,g196)
    c: InternalAlignment(g194,g196)
    c: InternalAlignment(g195,g196)
    c: InternalAlignment(g197,g196)
    c: InternalAlignment(g198,g196)
    c: Weight(g199) = 1
    c: Equal(g199,g200)
    c: Equal(g199,g201)
    c: InternalAlignment(g199,g202)
    c: InternalAlignment(g200,g202)
    c: InternalAlignment(g201,g202)
    c: InternalAlignment(g203,g202)
    c: InternalAlignment(g204,g202)
    c: Block(g202)
    c: Block(g196)
    c: Coincident(g205,g202)
    c: Coincident(g205,g37)
    c: Coincident(g206,g37)
    c: Coincident(g206,g196)
    c: Coincident(g207,g196)
    c: Coincident(g207,g202)
    c: Vertical(g207)
    c: Weight(g208) = 1
    c: Equal(g208,g209)
    c: Equal(g208,g210)
    c: InternalAlignment(g208,g211)
    c: InternalAlignment(g209,g211)
    c: InternalAlignment(g210,g211)
    c: InternalAlignment(g212,g211)
    c: InternalAlignment(g213,g211)
    c: Weight(g214) = 1
    c: Equal(g214,g215)
    c: Equal(g214,g216)
    c: InternalAlignment(g214,g217)
    c: InternalAlignment(g215,g217)
    c: InternalAlignment(g216,g217)
    c: InternalAlignment(g218,g217)
    c: InternalAlignment(g219,g217)
    c: Block(g217)
    c: Block(g211)
    c: Coincident(g220,g211)
    c: Coincident(g220,g43)
    c: Coincident(g221,g43)
    c: Coincident(g221,g217)
    c: Coincident(g222,g217)
    c: Coincident(g222,g211)
    c: Vertical(g222)
    c: Horizontal(g223)
    c: Block(g223)
    c: Vertical(g224)
    c: Block(g224)
    c: Block(g225)
    c: Weight(g226) = 1
    c: Equal(g226,g227)
    c: Equal(g226,g228)
    c: InternalAlignment(g226,g229)
    c: InternalAlignment(g227,g229)
    c: InternalAlignment(g228,g229)
    c: InternalAlignment(g230,g229)
    c: InternalAlignment(g231,g229)
    c: Weight(g232) = 1
    c: Equal(g232,g233)
    c: Equal(g232,g234)
    c: InternalAlignment(g232,g235)
    c: InternalAlignment(g233,g235)
    c: InternalAlignment(g234,g235)
    c: InternalAlignment(g236,g235)
    c: InternalAlignment(g237,g235)
    c: Weight(g238) = 1
    c: Equal(g238,g239)
    c: Equal(g238,g240)
    c: InternalAlignment(g238,g241)
    c: InternalAlignment(g239,g241)
    c: InternalAlignment(g240,g241)
    c: InternalAlignment(g242,g241)
    c: InternalAlignment(g243,g241)
    c: Weight(g244) = 1
    c: Equal(g244,g245)
    c: Equal(g244,g246)
    c: InternalAlignment(g244,g247)
    c: InternalAlignment(g245,g247)
    c: InternalAlignment(g246,g247)
    c: InternalAlignment(g248,g247)
    c: InternalAlignment(g249,g247)
    c: Block(g229)
    c: Block(g235)
    c: Block(g241)
    c: Block(g247)
    c: Coincident(g250,g235)
    c: Coincident(g250,g229)
    c: Horizontal(g250)
    c: Block(g192)
    c: Weight(g251) = 1
    c: Equal(g251,g252)
    c: Equal(g251,g253)
    c: InternalAlignment(g251,g254)
    c: InternalAlignment(g252,g254)
    c: InternalAlignment(g253,g254)
    c: InternalAlignment(g255,g254)
    c: InternalAlignment(g256,g254)
    c: Weight(g257) = 1
    c: Equal(g257,g258)
    c: Equal(g257,g259)
    c: InternalAlignment(g257,g260)
    c: InternalAlignment(g258,g260)
    c: InternalAlignment(g259,g260)
    c: InternalAlignment(g261,g260)
    c: InternalAlignment(g262,g260)
    c: Block(g254)
    c: Block(g260)
    c: Coincident(g263,g254)
    c: Coincident(g263,g260)
    c: Weight(g264) = 1
    c: Equal(g264,g265)
    c: Equal(g264,g266)
    c: InternalAlignment(g264,g267)
    c: InternalAlignment(g265,g267)
    c: InternalAlignment(g266,g267)
    c: InternalAlignment(g268,g267)
    c: InternalAlignment(g269,g267)
    c: Weight(g270) = 1
    c: Equal(g270,g271)
    c: Equal(g270,g272)
    c: InternalAlignment(g270,g273)
    c: InternalAlignment(g271,g273)
    c: InternalAlignment(g272,g273)
    c: InternalAlignment(g274,g273)
    c: InternalAlignment(g275,g273)
    c: Weight(g276) = 1
    c: Equal(g276,g277)
    c: Equal(g276,g278)
    c: InternalAlignment(g276,g279)
    c: InternalAlignment(g277,g279)
    c: InternalAlignment(g278,g279)
    c: InternalAlignment(g280,g279)
    c: InternalAlignment(g281,g279)
    c: Block(g279)
    c: Block(g273)
    c: Block(g267)
    c: Coincident(g282,g273)
    c: Coincident(g282,g267)
    c: Coincident(g283,g267)
    c: Coincident(g283,g279)
    c: Vertical(g283)
    c: Coincident(g284,g279)
    c: Coincident(g284,g273)
    c: Horizontal(g284)
    c: Weight(g285) = 1
    c: Equal(g285,g286)
    c: Equal(g285,g287)
    c: InternalAlignment(g285,g288)
    c: InternalAlignment(g286,g288)
    c: InternalAlignment(g287,g288)
    c: InternalAlignment(g289,g288)
    c: InternalAlignment(g290,g288)
    c: Weight(g291) = 1
    c: Equal(g291,g292)
    c: Equal(g291,g293)
    c: InternalAlignment(g291,g294)
    c: InternalAlignment(g292,g294)
    c: InternalAlignment(g293,g294)
    c: InternalAlignment(g295,g294)
    c: InternalAlignment(g296,g294)
    c: Weight(g297) = 1
    c: Equal(g297,g298)
    c: Equal(g297,g299)
    c: InternalAlignment(g297,g300)
    c: InternalAlignment(g298,g300)
    c: InternalAlignment(g299,g300)
    c: InternalAlignment(g301,g300)
    c: InternalAlignment(g302,g300)
    c: Block(g300)
    c: Block(g294)
    c: Block(g288)
    c: Coincident(g303,g300)
    c: Coincident(g303,g294)
    c: Horizontal(g303)
    c: Coincident(g304,g294)
    c: Coincident(g304,g288)
    c: Vertical(g304)
    c: Coincident(g305,g288)
    c: Coincident(g305,g300)
    c: InternalAlignment(g306,g307)
    c: InternalAlignment(g308,g307)
    c: InternalAlignment(g309,g307)
    c: Block(g307)
    c: Equal(g310,g311)
    c: Equal(g310,g312)
    c: InternalAlignment(g310,g313)
    c: InternalAlignment(g311,g313)
    c: InternalAlignment(g312,g313)
    c: InternalAlignment(g314,g313)
    c: InternalAlignment(g315,g313)
    c: Block(g313)
    c: Coincident(g316,g307)
    c: Horizontal(g316)
    c: Block(g316)
    c: Coincident(g317,g307)
    c: Coincident(g317,g260)
    c: Vertical(g317)
    c: Coincident(g318,g313)
    c: Coincident(g318,g254)
    c: Vertical(g318)
    c: Coincident(g320,g5)
    c: Coincident(g321,g5)
    c: Block(g319)
    c: Block(g5)
    c: Block(g321)
    c: Block(g320)
    c: Distance(g317) = 119.89
FEATURE [Sketcher::SketchObject] Sketch001
  FullyConstrained = true
  MapMode = 4
  Placement = pos=(0,0,0) rot=(0.57735,0.57735,0.57735;2.0944rad)
  Support = -> [Sketch]
  sketch-geometry (46):
    g0: BSplineCurve PolesCount=3 KnotsCount=2 Degree=2 IsPeriodic=0
    g1: ArcOfCircle CenterX=73.1223 CenterY=-32.291 CenterZ=0 NormalX=0 NormalY=0 NormalZ=1 AngleXU=0 Radius=13 StartAngle=5.92268 EndAngle=9.06428
    g2: ArcOfCircle CenterX=66.7816 CenterY=-49.1439 CenterZ=0 NormalX=0 NormalY=0 NormalZ=1 AngleXU=0 Radius=13 StartAngle=2.78068 EndAngle=5.92131
    g3: ArcOfCircle CenterX=55.9263 CenterY=-78.1807 CenterZ=0 NormalX=0 NormalY=0 NormalZ=1 AngleXU=0 Radius=13 StartAngle=5.92268 EndAngle=9.06428
    g4: ArcOfCircle CenterX=49.5884 CenterY=-95.0342 CenterZ=0 NormalX=0 NormalY=0 NormalZ=1 AngleXU=0 Radius=13 StartAngle=2.78068 EndAngle=5.92131
    g5: ArcOfCircle CenterX=38.7206 CenterY=-124.067 CenterZ=0 NormalX=0 NormalY=0 NormalZ=1 AngleXU=0 Radius=13 StartAngle=5.92268 EndAngle=9.06428
    g6: ArcOfCircle CenterX=32.3875 CenterY=-140.92 CenterZ=0 NormalX=0 NormalY=0 NormalZ=1 AngleXU=0 Radius=13 StartAngle=2.78068 EndAngle=5.92131
    g7: ArcOfCircle CenterX=21.4715 CenterY=-169.934 CenterZ=0 NormalX=0 NormalY=0 NormalZ=1 AngleXU=0 Radius=13 StartAngle=5.92268 EndAngle=9.06428
    g8: ArcOfCircle CenterX=15.1336 CenterY=-186.787 CenterZ=0 NormalX=0 NormalY=0 NormalZ=1 AngleXU=0 Radius=13 StartAngle=2.78068 EndAngle=5.92131
    g9-g12: Circle x4 (B-spline internal-alignment scaffolding for g13; pole/knot coordinates omitted)
    g13: BSplineCurve PolesCount=4 KnotsCount=2 Degree=3 IsPeriodic=0
    g14: GeomPoint X=28.8094 Y=-19.0875 Z=0
    g15: GeomPoint X=47.0443 Y=-50.4712 Z=0
    g16: Circle CenterX=53.5586 CenterY=-23.2695 CenterZ=0 NormalX=0 NormalY=0 NormalZ=1 AngleXU=0 Radius=3.24518
    g17: Circle CenterX=-195.441 CenterY=-127.082 CenterZ=0 NormalX=0 NormalY=0 NormalZ=1 AngleXU=0 Radius=1
    g18: Circle CenterX=-8.24091 CenterY=-197.481 CenterZ=0 NormalX=0 NormalY=0 NormalZ=1 AngleXU=0 Radius=1
    g19: Circle CenterX=12.8789 CenterY=-141.321 CenterZ=0 NormalX=0 NormalY=0 NormalZ=1 AngleXU=0 Radius=1
    g20: BSplineCurve PolesCount=3 KnotsCount=2 Degree=2 IsPeriodic=0
    g21: GeomPoint X=-195.441 Y=-127.082 Z=0
    g22: GeomPoint X=12.8789 Y=-141.321 Z=0
    g23: Circle CenterX=-12.8016 CenterY=-179.036 CenterZ=0 NormalX=0 NormalY=0 NormalZ=1 AngleXU=0 Radius=10.5072
    g24: Circle CenterX=0.933922 CenterY=-166.43 CenterZ=0 NormalX=0 NormalY=0 NormalZ=1 AngleXU=0 Radius=3.26661
    g25: Circle CenterX=-33.5518 CenterY=-176.44 CenterZ=0 NormalX=0 NormalY=0 NormalZ=1 AngleXU=0 Radius=5.64388
    g26: Circle CenterX=-47.2366 CenterY=-173.859 CenterZ=0 NormalX=0 NormalY=0 NormalZ=1 AngleXU=0 Radius=3.01653
    g27: Circle CenterX=-56.2595 CenterY=-171.456 CenterZ=0 NormalX=0 NormalY=0 NormalZ=1 AngleXU=0 Radius=2.12826
    g28: ArcOfCircle CenterX=51.2151 CenterY=-198.473 CenterZ=0 NormalX=0 NormalY=0 NormalZ=1 AngleXU=0 Radius=20 StartAngle=2.78189 EndAngle=4.35269
    g29: LineSegment StartX=32.4951 StartY=-191.433 StartZ=0 EndX=94.6578 EndY=-26.1352 EndZ=0
    g30: LineSegment StartX=43.1192 StartY=-220.001 StartZ=0 EndX=-196.497 EndY=-129.89 EndZ=0
    g31: LineSegment StartX=43.1192 StartY=-220.001 StartZ=0 EndX=44.1752 EndY=-217.193 EndZ=0
    g32: LineSegment StartX=117.223 StartY=-19.0875 StartZ=0 EndX=117.223 EndY=-16.0875 EndZ=0
    g33: LineSegment StartX=117.223 StartY=-16.0875 StartZ=0 EndX=17.2232 EndY=-16.0875 EndZ=0
    g34: LineSegment StartX=17.2232 StartY=-16.0875 StartZ=0 EndX=17.2232 EndY=-19.0875 EndZ=0
    g35: LineSegment StartX=28.8094 StartY=-19.0875 StartZ=0 EndX=17.2232 EndY=-19.0875 EndZ=0
    g36: LineSegment StartX=47.0443 StartY=-50.4712 StartZ=0 EndX=12.8789 EndY=-141.321 EndZ=0
    g37: LineSegment StartX=-195.441 StartY=-127.082 StartZ=0 EndX=-196.497 EndY=-129.89 EndZ=0
    g38: LineSegment StartX=85.2866 StartY=-36.8766 StartZ=0 EndX=78.9396 EndY=-53.7463 EndZ=0
    g39: LineSegment StartX=60.9579 StartY=-27.7053 StartZ=0 EndX=54.6191 EndY=-44.5532 EndZ=0
    g40: LineSegment StartX=68.0907 StartY=-82.7664 StartZ=0 EndX=61.7465 EndY=-99.6365 EndZ=0
    g41: LineSegment StartX=43.7619 StartY=-73.595 StartZ=0 EndX=37.426 EndY=-90.4435 EndZ=0
    g42: LineSegment StartX=50.885 StartY=-128.652 StartZ=0 EndX=44.5456 EndY=-145.522 EndZ=0
    g43: LineSegment StartX=26.5562 StartY=-119.481 StartZ=0 EndX=20.2251 EndY=-136.329 EndZ=0
    g44: LineSegment StartX=9.3071 StartY=-165.349 StartZ=0 EndX=2.97115 EndY=-182.197 EndZ=0
    g45: LineSegment StartX=33.6358 StartY=-174.52 StartZ=0 EndX=27.2917 EndY=-191.39 EndZ=0
  constraints (71):
    c: Block(g0)
    c: Block(g1)
    c: Block(g2)
    c: Block(g4)
    c: Block(g3)
    c: Block(g6)
    c: Block(g5)
    c: Block(g8)
    c: Block(g7)
    c: Weight(g9) = 1
    c: Equal(g9,g10)
    c: Equal(g9,g11)
    c: Equal(g9,g12)
    c: InternalAlignment(g9-g12 -> g13) x4
    c: InternalAlignment(g14,g13)
    c: InternalAlignment(g15,g13)
    c: Block(g16)
    c: Weight(g17) = 1
    c: Equal(g17,g18)
    c: Equal(g17,g19)
    c: InternalAlignment(g17,g20)
    c: InternalAlignment(g18,g20)
    c: InternalAlignment(g19,g20)
    c: InternalAlignment(g21,g20)
    c: InternalAlignment(g22,g20)
    c: Block(g20)
    c: Block(g23)
    c: Block(g24)
    c: Block(g25)
    c: Block(g26)
    c: Block(g27)
    c: Block(g28)
    c: Coincident(g29,g28)
    c: Coincident(g29,g0)
    c: Block(g13)
    c: Coincident(g31,g30)
    c: Coincident(g31,g28)
    c: Block(g31)
    c: Coincident(g32,g0)
    c: Vertical(g32)
    c: Coincident(g33,g32)
    c: Horizontal(g33)
    c: Coincident(g34,g33)
    c: Vertical(g34)
    c: Block(g33)
    c: Coincident(g35,g13)
    c: Coincident(g35,g34)
    c: Horizontal(g35)
    c: Coincident(g36,g13)
    c: Coincident(g36,g20)
    c: Coincident(g37,g20)
    c: Coincident(g37,g30)
    c: Block(g30)
    c: Coincident(g38,g1)
    c: Coincident(g38,g2)
    c: Coincident(g39,g1)
    c: Coincident(g39,g2)
    c: Coincident(g40,g3)
    c: Coincident(g40,g4)
    c: Coincident(g41,g3)
    c: Coincident(g41,g4)
    c: Coincident(g42,g5)
    c: Coincident(g42,g6)
    c: Coincident(g43,g5)
    c: Coincident(g43,g6)
    c: Coincident(g44,g7)
    c: Coincident(g44,g8)
    c: Coincident(g45,g7)
    c: Coincident(g45,g8)
    c: Distance(g30) = 256
    c: Distance(g33) = 100
FEATURE [Part::Extrusion] Extrude002
  Base = -> Sketch001
  Dir = (1,0,0)
  DirMode = 2
  FaceMakerClass = Part::FaceMakerBullseye
  LengthFwd = 8
  LengthRev = 0
  Solid = true
  Symmetric = false
FEATURE [Sketcher::SketchObject] Sketch002
  FullyConstrained = true
  sketch-geometry (20):
    g0: LineSegment StartX=-2.77179 StartY=-200.304 StartZ=0 EndX=5.22821 EndY=-200.304 EndZ=0
    g1: LineSegment StartX=5.22821 StartY=-200.304 StartZ=0 EndX=5.22821 EndY=-197.304 EndZ=0
    g2: LineSegment StartX=-2.77179 StartY=-200.304 StartZ=0 EndX=-2.77179 EndY=-197.304 EndZ=0
    g3: LineSegment StartX=5.22821 StartY=-197.304 StartZ=0 EndX=8.22821 EndY=-197.304 EndZ=0
    g4: LineSegment StartX=-2.77179 StartY=-197.304 StartZ=0 EndX=-5.77179 EndY=-197.304 EndZ=0
    g5: LineSegment StartX=19.2282 StartY=-203.304 StartZ=0 EndX=19.2282 EndY=-206.304 EndZ=0
    g6: LineSegment StartX=-16.7718 StartY=-203.304 StartZ=0 EndX=-16.7718 EndY=-206.304 EndZ=0
    g7: LineSegment StartX=-16.7718 StartY=-206.304 StartZ=0 EndX=19.2282 EndY=-206.304 EndZ=0
    g8: Circle CenterX=-16.7718 CenterY=-203.304 CenterZ=0 NormalX=0 NormalY=0 NormalZ=1 AngleXU=0 Radius=1
    g9: Circle CenterX=-5.77179 CenterY=-203.304 CenterZ=0 NormalX=0 NormalY=0 NormalZ=1 AngleXU=0 Radius=1
    g10: Circle CenterX=-5.77179 CenterY=-197.304 CenterZ=0 NormalX=0 NormalY=0 NormalZ=1 AngleXU=0 Radius=1
    g11: BSplineCurve PolesCount=3 KnotsCount=2 Degree=2 IsPeriodic=0
    g12: GeomPoint X=-16.7718 Y=-203.304 Z=0
    g13: GeomPoint X=-5.77179 Y=-197.304 Z=0
    g14: Circle CenterX=19.2282 CenterY=-203.304 CenterZ=0 NormalX=0 NormalY=0 NormalZ=1 AngleXU=0 Radius=1
    g15: Circle CenterX=8.22821 CenterY=-203.304 CenterZ=0 NormalX=0 NormalY=0 NormalZ=1 AngleXU=0 Radius=1
    g16: Circle CenterX=8.22821 CenterY=-197.304 CenterZ=0 NormalX=0 NormalY=0 NormalZ=1 AngleXU=0 Radius=1
    g17: BSplineCurve PolesCount=3 KnotsCount=2 Degree=2 IsPeriodic=0
    g18: GeomPoint X=19.2282 Y=-203.304 Z=0
    g19: GeomPoint X=8.22821 Y=-197.304 Z=0
  constraints (41):
    c: Horizontal(g0)
    c: Distance(g0) = 8
    c: Coincident(g1,g0)
    c: Vertical(g1)
    c: Distance(g1) = 3
    c: Coincident(g2,g0)
    c: Vertical(g2)
    c: Distance(g2) = 3
    c: Coincident(g3,g1)
    c: Horizontal(g3)
    c: Distance(g3) = 3
    c: Coincident(g4,g2)
    c: Horizontal(g4)
    c: Distance(g4) = 3
    c: Vertical(g5)
    c: Vertical(g6)
    c: Coincident(g7,g6)
    c: Coincident(g7,g5)
    c: Weight(g8) = 1
    c: Equal(g8,g9)
    c: Equal(g8,g10)
    c: Coincident(g11,g4)
    c: InternalAlignment(g8,g11)
    c: InternalAlignment(g9,g11)
    c: InternalAlignment(g10,g11)
    c: InternalAlignment(g12,g11)
    c: InternalAlignment(g13,g11)
    c: Coincident(g17,g5)
    c: Weight(g14) = 1
    c: Equal(g14,g15)
    c: Equal(g14,g16)
    c: Coincident(g17,g3)
    c: InternalAlignment(g14,g17)
    c: InternalAlignment(g15,g17)
    c: InternalAlignment(g16,g17)
    c: InternalAlignment(g18,g17)
    c: InternalAlignment(g19,g17)
    c: Block(g7)
    c: Block(g17)
    c: Block(g11)
    c: Block(g6)
FEATURE [Part::Extrusion] Extrude003
  Base = -> Sketch002
  Dir = (0,0,1)
  DirMode = 2
  FaceMakerClass = Part::FaceMakerBullseye
  LengthFwd = 260
  LengthRev = 0
  Solid = true
  Symmetric = false
FEATURE [Part::Extrusion] Extrude
  Base = -> Sketch
  Dir = (0,0,1)
  DirMode = 2
  FaceMakerClass = Part::FaceMakerBullseye
  LengthFwd = 14
  LengthRev = 0
  Solid = true
  Symmetric = false
